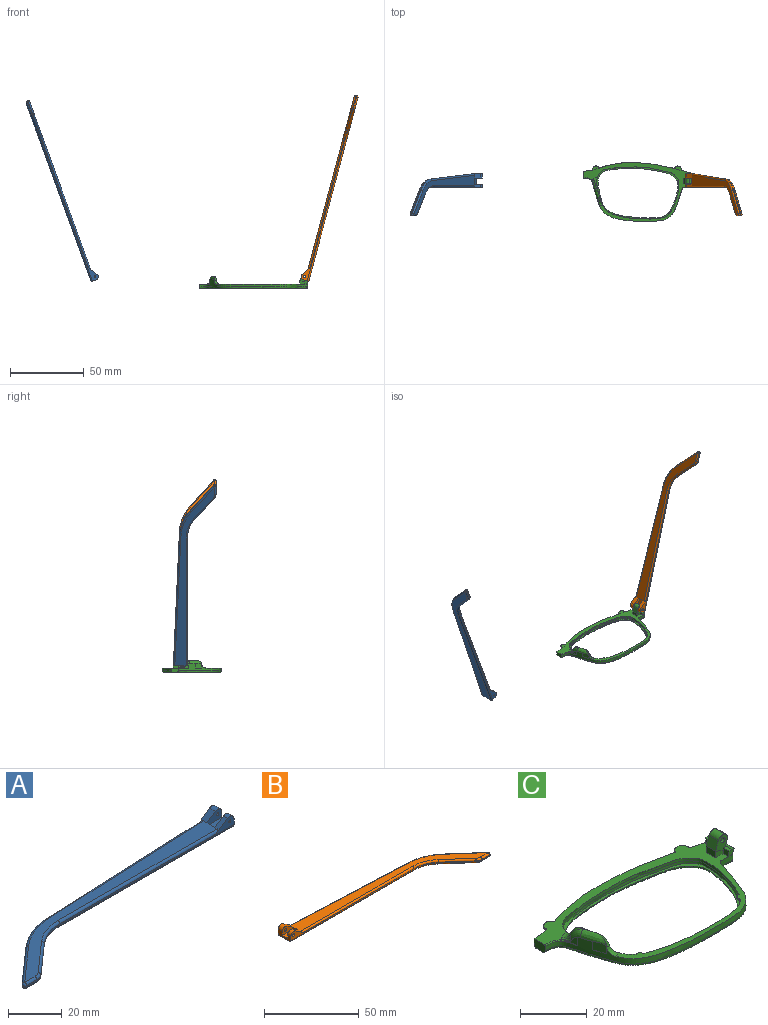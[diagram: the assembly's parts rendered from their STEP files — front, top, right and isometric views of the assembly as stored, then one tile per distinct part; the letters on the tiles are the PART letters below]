
ASSEMBLY  parts=3 mates=1
PART A: 43 faces, bbox 130.2x29.5x5.9 mm
  f0: plane 9.62x3.72mm, normal (1,0,0), area 24.7mm2, adj f1,f3,f4,f5,f10,f16,f18,f28
  f1: cylinder r=2.2mm len=3.45mm, axis (0,-1,0), area 11mm2, adj f0,f2,f4,f37
  f2: plane 6.01x3.91mm, normal (-0.55,0,0.84), area 12.7mm2, adj f1,f4,f9,f19,f37
  f3: plane 2.26x0.1mm, normal (0,0,1), area 0.1mm2, adj f0,f5,f18
  f4: plane 92.1x4.9mm, normal (0,-1,0), area 79.9mm2, adj f0,f1,f2,f14,f19,f36,f42
  f5: plane 93.42x4.13mm, normal (-0.04,1,0), area 64.8mm2, adj f0,f3,f11,f15,f17,f27,f28
  f6: plane 17.82x15.72mm, normal (-0.66,0.75,0), area 14.3mm2, adj f11,f12,f25,f30
  f7: plane 5.46x0.6mm, normal (0,-1,0), area 3.3mm2, adj f12,f13,f23,f32
  f8: plane 14.99x13.23mm, normal (0.66,-0.75,0), area 12mm2, adj f13,f14,f21,f34
  f9: plane 121.18x26.73mm, normal (0,0,1), area 627.7mm2, adj f2,f17,f19,f20,f21,f22,f23,f25
  f10: plane 129.1x27.08mm, normal (0,0,-1), area 686.5mm2, adj f0,f28,f29,f30,f32,f33,f34,f35
  f11: cylinder r=30mm len=18.52mm, axis (0,0,-1), area 12.2mm2, adj f5,f6,f26,f29
  f12: cylinder r=1mm len=1.75mm, axis (0,0,-1), area 1.5mm2, adj f6,f7,f24,f31
  f13: cylinder r=5mm len=3.31mm, axis (0,0,-1), area 2.2mm2, adj f7,f8,f22,f33
  f14: cylinder r=20mm len=13.23mm, axis (0,0,1), area 8.7mm2, adj f4,f8,f20,f35
  f15: plane 5.66x0.25mm, normal (0,0,-1), area 0.7mm2, adj f5,f17,f18
  f16: cylinder r=2.2mm len=3.45mm, axis (0,-1,0), area 14.8mm2, adj f0,f17,f18,f38
  f17: plane 6.01x3.91mm, normal (-0.55,0,0.84), area 16.9mm2, adj f5,f9,f15,f16,f18,f27,f38
  f18: plane 7.92x3.3mm, normal (0,1,0), area 15.9mm2, adj f0,f3,f15,f16,f17,f41
  f19: cylinder r=1mm len=84.18mm, axis (-1,0,0), area 131.4mm2, adj f2,f4,f9,f20
  f20: torus R=21mm, axis (0,0,1), area 23.1mm2, adj f9,f14,f19,f21
  f21: cylinder r=1mm len=15.65mm, axis (-0.75,-0.66,0), area 31.4mm2, adj f8,f9,f20,f22
  f22: torus R=4mm, axis (0,0,1), area 5.3mm2, adj f9,f13,f21,f23
  f23: cylinder r=1mm len=5.46mm, axis (-1,0,0), area 8.6mm2, adj f7,f9,f22,f24
  f24: sphere r=1mm, area 2.4mm2, adj f12,f23,f25
  f25: cylinder r=1mm len=18.48mm, axis (0.75,0.66,0), area 37.3mm2, adj f6,f9,f24,f26
  f26: torus R=29mm, axis (0,0,1), area 31.6mm2, adj f9,f11,f25,f27
  f27: cylinder r=1mm len=85.5mm, axis (1,0.04,0), area 133.5mm2, adj f5,f9,f17,f26
  f28: cylinder r=1mm len=93.46mm, axis (-1,-0.04,0), area 146.9mm2, adj f0,f5,f10,f29
  f29: torus R=29mm, axis (0,0,1), area 31.6mm2, adj f10,f11,f28,f30
  f30: cylinder r=1mm len=18.48mm, axis (-0.75,-0.66,0), area 37.3mm2, adj f6,f10,f29,f31
  f31: sphere r=1mm, area 2.4mm2, adj f12,f30,f32
  f32: cylinder r=1mm len=5.46mm, axis (1,0,0), area 8.6mm2, adj f7,f10,f31,f33
  f33: torus R=4mm, axis (0,0,1), area 5.3mm2, adj f10,f13,f32,f34
  f34: cylinder r=1mm len=15.65mm, axis (0.75,0.66,0), area 31.4mm2, adj f8,f10,f33,f35
  f35: torus R=21mm, axis (0,0,1), area 23.1mm2, adj f10,f14,f34,f36
  f36: cylinder r=1mm len=92.1mm, axis (1,0,0), area 144.7mm2, adj f0,f4,f10,f35
  f37: plane 7.92x4.7mm, normal (0,1,0), area 27mm2, adj f0,f1,f2,f39,f40,f42
  f38: plane 7.92x4.7mm, normal (0,-1,0), area 27mm2, adj f0,f16,f17,f39,f40,f41
  f39: plane 7.92x4.1mm, normal (0,0,1), area 32.5mm2, adj f0,f37,f38,f40
  f40: plane 4.1x1.4mm, normal (1,0,0), area 5.7mm2, adj f9,f37,f38,f39
  f41: cylinder r=0.5mm len=3.1mm, axis (0,-1,0), area 9.7mm2, adj f18,f38
  f42: cylinder r=0.5mm len=2.3mm, axis (0,-1,0), area 7.2mm2, adj f4,f37
PART B: 43 faces, bbox 130.2x29.5x5.9 mm
  f0: plane 9.62x3.72mm, normal (-1,0,0), area 24.7mm2, adj f1,f3,f4,f5,f10,f16,f18,f28
  f1: cylinder r=2.2mm len=3.45mm, axis (0,-1,0), area 11mm2, adj f0,f2,f4,f37
  f2: plane 6.01x3.91mm, normal (0.55,0,0.84), area 12.7mm2, adj f1,f4,f9,f19,f37
  f3: plane 2.26x0.1mm, normal (0,0,1), area 0.1mm2, adj f0,f5,f18
  f4: plane 92.1x4.9mm, normal (0,-1,0), area 78.2mm2, adj f0,f1,f2,f14,f19,f36,f42
  f5: plane 93.42x4.13mm, normal (0.04,1,0), area 64.8mm2, adj f0,f3,f11,f15,f17,f27,f28
  f6: plane 17.82x15.72mm, normal (0.66,0.75,0), area 14.3mm2, adj f11,f12,f25,f30
  f7: plane 5.46x0.6mm, normal (0,-1,0), area 3.3mm2, adj f12,f13,f23,f32
  f8: plane 14.99x13.23mm, normal (-0.66,-0.75,0), area 12mm2, adj f13,f14,f21,f34
  f9: plane 121.18x26.73mm, normal (0,0,1), area 627.7mm2, adj f2,f17,f19,f20,f21,f22,f23,f25
  f10: plane 129.1x27.08mm, normal (0,0,-1), area 686.5mm2, adj f0,f28,f29,f30,f32,f33,f34,f35
  f11: cylinder r=30mm len=18.52mm, axis (0,0,-1), area 12.2mm2, adj f5,f6,f26,f29
  f12: cylinder r=1mm len=1.75mm, axis (0,0,-1), area 1.5mm2, adj f6,f7,f24,f31
  f13: cylinder r=5mm len=3.31mm, axis (0,0,-1), area 2.2mm2, adj f7,f8,f22,f33
  f14: cylinder r=20mm len=13.23mm, axis (0,0,1), area 8.7mm2, adj f4,f8,f20,f35
  f15: plane 5.66x0.25mm, normal (0,0,-1), area 0.7mm2, adj f5,f17,f18
  f16: cylinder r=2.2mm len=3.45mm, axis (0,-1,0), area 14.8mm2, adj f0,f17,f18,f38
  f17: plane 6.01x3.91mm, normal (0.55,0,0.84), area 16.9mm2, adj f5,f9,f15,f16,f18,f27,f38
  f18: plane 7.92x3.3mm, normal (0,1,0), area 14.3mm2, adj f0,f3,f15,f16,f17,f41
  f19: cylinder r=1mm len=84.18mm, axis (1,0,0), area 131.4mm2, adj f2,f4,f9,f20
  f20: torus R=21mm, axis (0,0,1), area 23.1mm2, adj f9,f14,f19,f21
  f21: cylinder r=1mm len=15.65mm, axis (0.75,-0.66,0), area 31.4mm2, adj f8,f9,f20,f22
  f22: torus R=4mm, axis (0,0,1), area 5.3mm2, adj f9,f13,f21,f23
  f23: cylinder r=1mm len=5.46mm, axis (1,0,0), area 8.6mm2, adj f7,f9,f22,f24
  f24: sphere r=1mm, area 2.4mm2, adj f12,f23,f25
  f25: cylinder r=1mm len=18.48mm, axis (-0.75,0.66,0), area 37.3mm2, adj f6,f9,f24,f26
  f26: torus R=29mm, axis (0,0,1), area 31.6mm2, adj f9,f11,f25,f27
  f27: cylinder r=1mm len=85.5mm, axis (-1,0.04,0), area 133.5mm2, adj f5,f9,f17,f26
  f28: cylinder r=1mm len=93.46mm, axis (1,-0.04,0), area 146.9mm2, adj f0,f5,f10,f29
  f29: torus R=29mm, axis (0,0,1), area 31.6mm2, adj f10,f11,f28,f30
  f30: cylinder r=1mm len=18.48mm, axis (0.75,-0.66,0), area 37.3mm2, adj f6,f10,f29,f31
  f31: sphere r=1mm, area 2.4mm2, adj f12,f30,f32
  f32: cylinder r=1mm len=5.46mm, axis (-1,0,0), area 8.6mm2, adj f7,f10,f31,f33
  f33: torus R=4mm, axis (0,0,1), area 5.3mm2, adj f10,f13,f32,f34
  f34: cylinder r=1mm len=15.65mm, axis (-0.75,0.66,0), area 31.4mm2, adj f8,f10,f33,f35
  f35: torus R=21mm, axis (0,0,1), area 23.1mm2, adj f10,f14,f34,f36
  f36: cylinder r=1mm len=92.1mm, axis (-1,0,0), area 144.7mm2, adj f0,f4,f10,f35
  f37: plane 7.92x4.7mm, normal (0,1,0), area 25.4mm2, adj f0,f1,f2,f39,f40,f42
  f38: plane 7.92x4.7mm, normal (0,-1,0), area 25.4mm2, adj f0,f16,f17,f39,f40,f41
  f39: plane 7.92x4.1mm, normal (0,0,1), area 32.5mm2, adj f0,f37,f38,f40
  f40: plane 4.1x1.4mm, normal (-1,0,0), area 5.7mm2, adj f9,f37,f38,f39
  f41: cylinder r=0.88mm len=3.1mm, axis (0,-1,0), area 17mm2, adj f18,f38
  f42: cylinder r=0.88mm len=2.3mm, axis (0,-1,0), area 12.6mm2, adj f4,f37
PART C: 61 faces, bbox 75.1x40.9x17.9 mm
  f0: bspline ~1.82x1.22mm, area 0.7mm2, adj f2,f7,f38,f53
  f1: plane 74.08x40.46mm, normal (0,0,1), area 432.2mm2, adj f4,f5,f6,f7,f8,f9,f13,f21
  f2: bspline ~6.1x4.93mm, area 12.7mm2, adj f0,f7,f38,f42,f44,f53,f54
  f3: plane 4.46x1.45mm, normal (0,0,1), area 0.1mm2, adj f7,f39
  f4: plane 1.23x0.04mm, normal (0,0,1), area 0mm2, adj f1,f7,f23
  f5: plane 6.97x5.07mm, normal (0,1,0), area 22.7mm2, adj f1,f21,f22,f26,f28,f29,f31,f32
  f6: plane 3.2x2.36mm, normal (0,-1,0), area 5.7mm2, adj f1,f21,f27,f30
  f7: extruded ~73.26x39.84mm, area 290.5mm2, adj f0,f1,f2,f3,f4,f8,f9,f14
  f8: extruded ~35.39x5.69mm, area 69.9mm2, adj f1,f7,f9,f19,f45,f46
  f9: plane 4.83x3.04mm, normal (-1,0,0), area 13.9mm2, adj f1,f7,f8,f10,f14,f19,f58
  f10: plane 72.4x37.85mm, normal (0,0,-1), area 291.2mm2, adj f9,f14,f16,f18,f19,f20
  f11: plane 56.06x35.45mm, normal (0,0,1), area 127mm2, adj f12,f20
  f12: extruded ~55.69x35.36mm, area 160.5mm2, adj f11,f13
  f13: extruded ~55.69x35.36mm, area 229.5mm2, adj f1,f12,f40,f41,f42,f43,f44,f49
  f14: bspline ~73.27x30.39mm, area 161.7mm2, adj f7,f9,f10,f15
  f15: bspline ~1x1mm, area 0.8mm2, adj f7,f14,f16
  f16: bspline ~8.99x1.23mm, area 12.6mm2, adj f7,f10,f15,f17
  f17: bspline ~1.04x1mm, area 0.7mm2, adj f7,f16,f18
  f18: bspline ~45.86x8.59mm, area 59.8mm2, adj f7,f10,f17,f19
  f19: bspline ~37.01x6.7mm, area 56.6mm2, adj f8,f9,f10,f18
  f20: bspline ~56.23x35.9mm, area 235.3mm2, adj f10,f11
  f21: plane 4x2.36mm, normal (-1,0,0), area 9.5mm2, adj f1,f5,f6,f22
  f22: plane 4x0.02mm, normal (0.34,0,0.94), area 0.1mm2, adj f5,f21,f29
  f23: plane 2.76x2.53mm, normal (0,-1,0), area 3.9mm2, adj f4,f27,f28,f36,f57
  f24: plane 7.67x1.6mm, normal (0.94,0,-0.34), area 13mm2, adj f1,f36,f37,f57
  f25: plane 2.1x1.69mm, normal (0,1,0), area 2.8mm2, adj f1,f26,f28,f37,f57
  f26: plane 3.3x2.1mm, normal (-1,0,0), area 6.9mm2, adj f1,f5,f25,f28
  f27: plane 2.35x2.1mm, normal (-1,0,0), area 4.9mm2, adj f1,f6,f23,f28,f30
  f28: plane 9.65x1.24mm, normal (0,0,1), area 8.2mm2, adj f5,f23,f25,f26,f27,f30,f31,f57
  f29: plane 4x3.31mm, normal (-0.94,0,0.34), area 14.1mm2, adj f5,f22,f30,f33
  f30: plane 5.77x5.06mm, normal (0,-1,0), area 17mm2, adj f6,f27,f28,f29,f31,f32,f33,f34
  f31: plane 4x2.21mm, normal (0.94,0,-0.34), area 9.4mm2, adj f5,f28,f30,f34
  f32: plane 4x0.01mm, normal (0.34,0,0.94), area 0mm2, adj f5,f30,f33,f34
  f33: cylinder r=1.98mm len=4mm, axis (0,1,0), area 12.4mm2, adj f5,f29,f30,f32
  f34: cylinder r=1.98mm len=4mm, axis (0,-1,0), area 12.4mm2, adj f5,f30,f31,f32
  f35: cylinder r=0.88mm len=4mm, axis (0,-1,0), area 22mm2, adj f5,f30
  f36: cone r=1mm half-angle=20deg, axis (0,0,1), area 2.3mm2, adj f1,f23,f24,f57
  f37: cylinder r=1mm len=2.28mm, axis (-0.34,0,-0.94), area 3mm2, adj f1,f24,f25,f57
  f38: extruded ~3.67x3.11mm, area 5.9mm2, adj f0,f2,f7,f60
  f39: extruded ~4.44x3.32mm, area 15.1mm2, adj f3,f7,f43,f44,f56
  f40: extruded ~4.98x1.37mm, area 6.6mm2, adj f13,f42
  f41: plane 3.63x0.97mm, normal (0,0,1), area 0.3mm2, adj f13,f42,f44
  f42: bspline ~15.5x15.35mm, area 6.4mm2, adj f2,f13,f40,f41,f55
  f43: bspline ~7.26x7.26mm, area 6.3mm2, adj f13,f39,f44,f56
  f44: bspline ~10.29x4.84mm, area 21.4mm2, adj f2,f7,f13,f39,f41,f43
  f45: plane 4.39x2.73mm, normal (0,0,-1), area 7.4mm2, adj f8,f46
  f46: cylinder r=2.28mm len=4.39mm, axis (0,0,1), area 3.4mm2, adj f1,f8,f45
  f47: cylinder r=2.28mm len=4.48mm, axis (0,0,1), area 3.6mm2, adj f1,f7,f48
  f48: plane 4.49x2.96mm, normal (0,0,-1), area 8.3mm2, adj f7,f47
  f49: plane 1.79x1.31mm, normal (0,0,-1), area 0.9mm2, adj f13,f50
  f50: cylinder r=1.3mm len=1.78mm, axis (0,0,1), area 1.3mm2, adj f1,f13,f49
  f51: plane 1.95x1.68mm, normal (0,0,-1), area 1.5mm2, adj f13,f52
  f52: cylinder r=1.3mm len=1.93mm, axis (0,0,1), area 1.5mm2, adj f1,f13,f51
  f53: bspline ~2.66x2.04mm, area 1.9mm2, adj f0,f2,f7,f54,f59
  f54: bspline ~3.55x3.47mm, area 3.7mm2, adj f1,f2,f53,f55,f59
  f55: bspline ~5.71x4.38mm, area 7.6mm2, adj f1,f13,f42,f54
  f56: bspline ~3.7x3.66mm, area 7.8mm2, adj f1,f7,f13,f39,f43
  f57: plane 9.71x1.44mm, normal (0.34,0,0.94), area 13.9mm2, adj f23,f24,f25,f28,f36,f37
  f58: bspline ~6.38x2.14mm, area 2.6mm2, adj f1,f7,f9,f59
  f59: bspline ~2.1x1.46mm, area 0.6mm2, adj f7,f53,f54,f58
  f60: bspline ~5.24x1.75mm, area 0mm2, adj f7,f38
PLACE A rot(axis=(0,1,0),70deg) t=(-84.77,-5.75,56)mm
PLACE B rot(axis=(0,-1,0),75deg) t=(68.2,-5.75,-61.61)mm
PLACE C t=(10.15,-1.13,-5.77)mm
MATE revolute B.f41 <-> C.f34  axis (0,-1,0) through (81.2,2.72,1.21)mm
